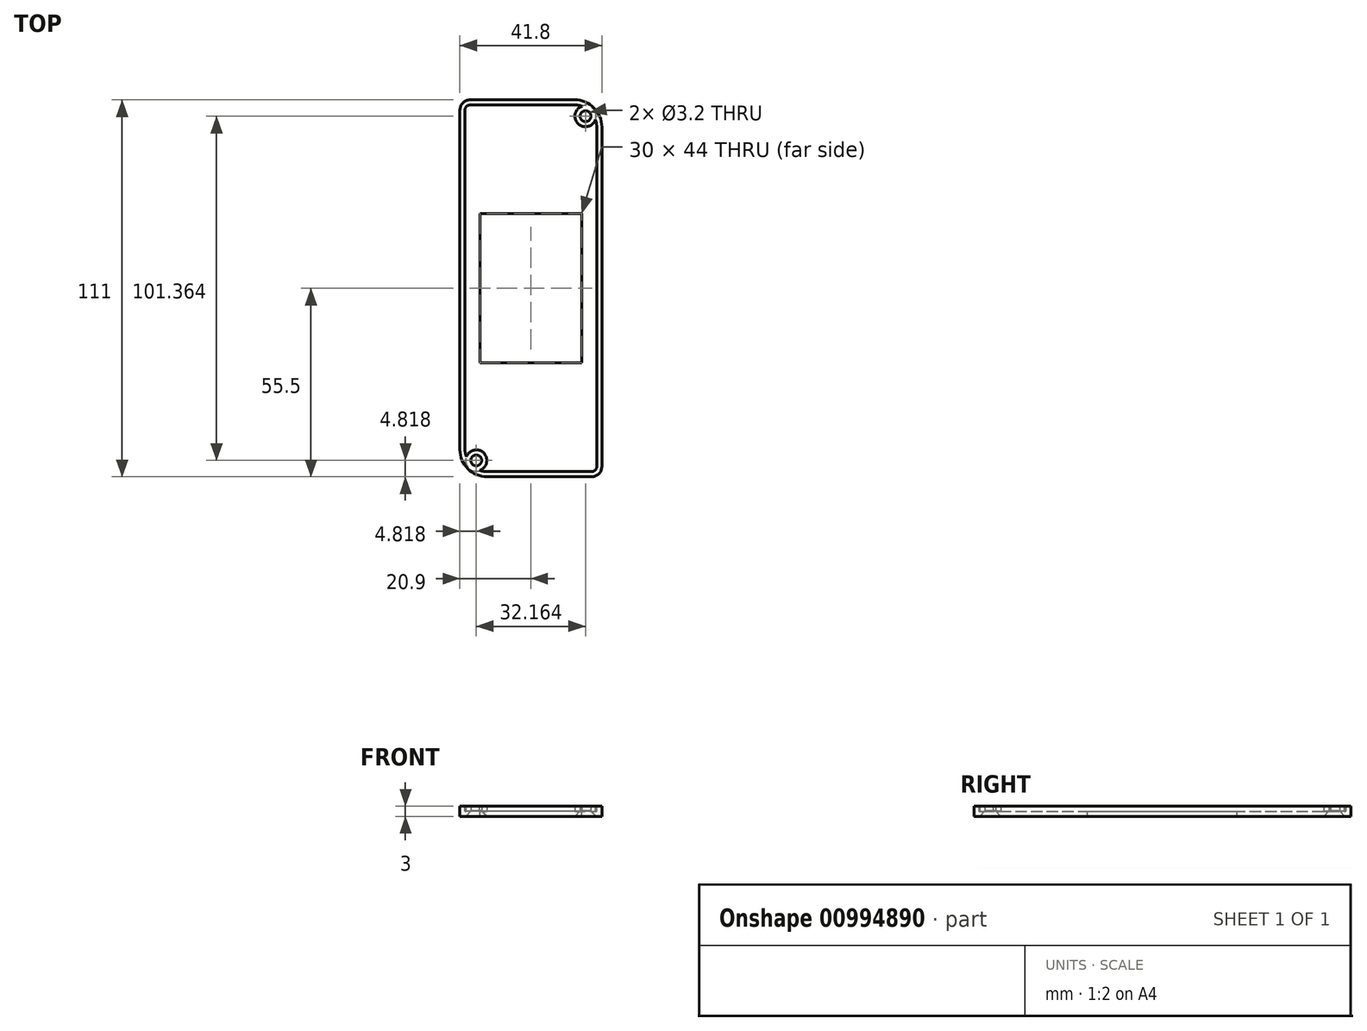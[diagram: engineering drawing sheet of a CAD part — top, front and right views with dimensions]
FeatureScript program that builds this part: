
annotation { "Feature Type Name" : "Feature", "Feature Type Description" : "" }
export const myFeature = defineFeature(function(context is Context, id is Id, definition is map)
    precondition{}
    {
        {
            var Q0;
            Q0=qCreatedBy(makeId("Top.planeOp"),FACE);
            var sketch = newSketch(context, id + "F0", { "sketchPlane" : qUnion([Q0])});
            skLineSegment(sketch, "E0.bottom", {"start": v(17.9, -55.5) * mm, "end": v(-12.9, -55.5) * mm});
            skLineSegment(sketch, "E0.top", {"start": v(12.9, 55.5) * mm, "end": v(-17.9, 55.5) * mm});
            skLineSegment(sketch, "E0.left", {"start": v(20.9, -52.5) * mm, "end": v(20.9, 47.5) * mm});
            skLineSegment(sketch, "E0.right", {"start": v(-20.9, -47.5) * mm, "end": v(-20.9, 52.5) * mm});
            skPoint(sketch, "E0.middle", {"position": v(0, 0) * mm});
            skPoint(sketch, "E1.visualSharp", {"position": v(-20.9, 55.5) * mm});
            skArc(sketch, "E1.filletArc", {"start": v(-17.9, 55.5) * mm, "mid": v(-20.02, 54.62) * mm, "end": v(-20.9, 52.5) * mm});
            skPoint(sketch, "E2.visualSharp", {"position": v(20.9, -55.5) * mm});
            skArc(sketch, "E2.filletArc", {"start": v(17.9, -55.5) * mm, "mid": v(20.02, -54.62) * mm, "end": v(20.9, -52.5) * mm});
            skPoint(sketch, "E3.visualSharp", {"position": v(20.9, 55.5) * mm});
            skArc(sketch, "E3.filletArc", {"start": v(20.9, 47.5) * mm, "mid": v(18.56, 53.16) * mm, "end": v(12.9, 55.5) * mm});
            skPoint(sketch, "E4.visualSharp", {"position": v(-20.9, -55.5) * mm});
            skArc(sketch, "E4.filletArc", {"start": v(-20.9, -47.5) * mm, "mid": v(-18.56, -53.16) * mm, "end": v(-12.9, -55.5) * mm});
            skLineSegment(sketch, "E5", {"start": v(20.9, 55.5) * mm, "end": v(12.9, 47.5) * mm, "construction": true});
            skLineSegment(sketch, "E6", {"start": v(-20.9, -55.5) * mm, "end": v(-12.9, -47.5) * mm, "construction": true});
            skCircle(sketch, "E7", {"center": v(16.08, 50.68) * mm, "radius": 1.6 * mm});
            skCircle(sketch, "E8", {"center": v(-16.08, -50.68) * mm, "radius": 1.6 * mm});
            skSolve(sketch);
        }
        {
            var Q0;
            Q0 = qSketchRegion(id + "F0", true);
            extrude(context, id + "F1", {"entities" : qUnion([Q0]), "depth" : 3 * mm, "offsetDistance" : 25 * mm});
        }
        {
            var Q0;
            Q0=makeQuery(id+"F1.opExtrude","CAP_FACE",FACE,{"disambiguationData":[OSD([sQuery(id+"F0.wireOp",EDGE,"E0.bottom"),sQuery(id+"F0.wireOp",EDGE,"E0.top"),sQuery(id+"F0.wireOp",EDGE,"E0.left"),sQuery(id+"F0.wireOp",EDGE,"E0.right"),sQuery(id+"F0.wireOp",EDGE,"E1.filletArc"),sQuery(id+"F0.wireOp",EDGE,"E2.filletArc"),sQuery(id+"F0.wireOp",EDGE,"E3.filletArc"),sQuery(id+"F0.wireOp",EDGE,"E4.filletArc")])],"isStart":false});
            shell(context, id + "F2", {"entities" : qUnion([Q0]), "thickness" : 1.5 * mm});
        }
        {
            var Q0;
            Q0=makeQuery(id+"F2.opShell","OFFSET_FACE",FACE,{"disambiguationData":[OSD([sQuery(id+"F0.wireOp",EDGE,"E0.bottom"),sQuery(id+"F0.wireOp",EDGE,"E0.top"),sQuery(id+"F0.wireOp",EDGE,"E0.left"),sQuery(id+"F0.wireOp",EDGE,"E0.right"),sQuery(id+"F0.wireOp",EDGE,"E1.filletArc"),sQuery(id+"F0.wireOp",EDGE,"E2.filletArc"),sQuery(id+"F0.wireOp",EDGE,"E3.filletArc"),sQuery(id+"F0.wireOp",EDGE,"E4.filletArc")])]});
            var sketch = newSketch(context, id + "F3", { "sketchPlane" : qUnion([Q0])});
            skLineSegment(sketch, "E9.bottom", {"start": v(15, -22) * mm, "end": v(-15, -22) * mm});
            skLineSegment(sketch, "E9.top", {"start": v(15, 22) * mm, "end": v(-15, 22) * mm});
            skLineSegment(sketch, "E9.left", {"start": v(15, -22) * mm, "end": v(15, 22) * mm});
            skLineSegment(sketch, "E9.right", {"start": v(-15, -22) * mm, "end": v(-15, 22) * mm});
            skPoint(sketch, "E9.middle", {"position": v(0, 0) * mm});
            skSolve(sketch);
        }
        {
            var Q0;
            Q0 = qSketchRegion(id + "F3", true);
            extrude(context, id + "F4", {"entities" : qUnion([Q0]), "operationType" : NewBodyOperationType.REMOVE, "endBound" : BoundingType.THROUGH_ALL, "oppositeDirection" : true, "depth" : 25 * mm, "offsetDistance" : 25 * mm});
        }
        {
            var Q0;
            Q0=makeQuery(id+"F1.opExtrude","CAP_EDGE",EDGE,{"disambiguationData":[OSD([sQuery(id+"F0.wireOp",EDGE,"E7")])],"isStart":true});
            var Q1;
            Q1=makeQuery(id+"F1.opExtrude","CAP_EDGE",EDGE,{"disambiguationData":[OSD([sQuery(id+"F0.wireOp",EDGE,"E8")])],"isStart":true});
            chamfer(context, id + "F5", {"entities" : qUnion([Q0, Q1]), "width" : 1.55 * mm, "tangentPropagation" : true});
        }
    });
